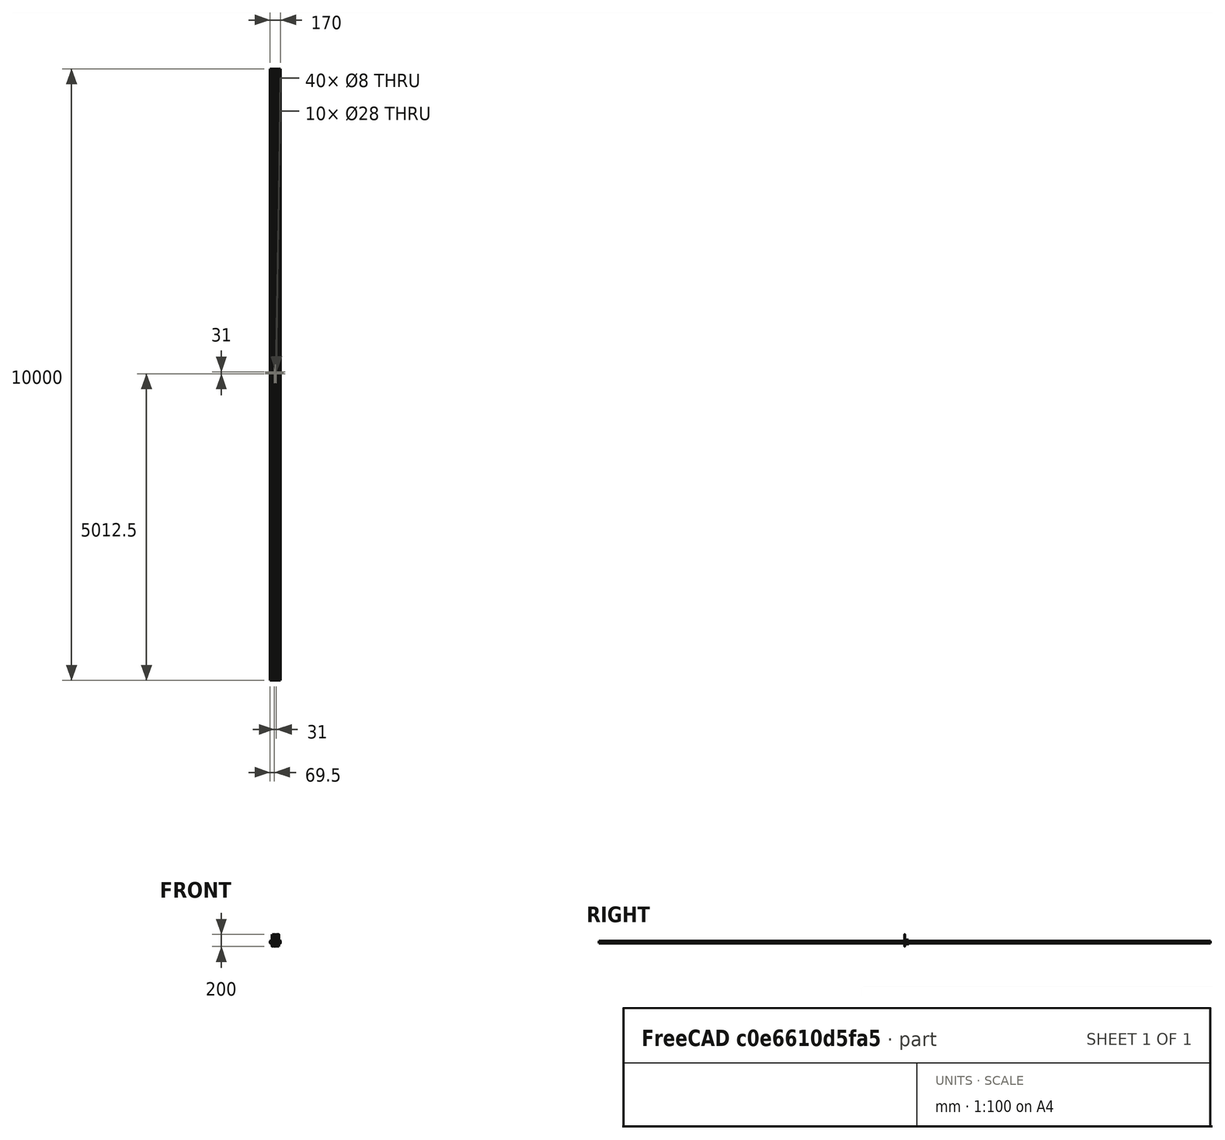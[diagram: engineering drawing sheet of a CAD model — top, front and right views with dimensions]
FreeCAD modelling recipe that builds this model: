
FCSTD DOCUMENT  (FreeCAD 0.16R6698 (Git))
Label: z_lower_left_v2.5
License: All rights reserved
LicenseURL: http://en.wikipedia.org/wiki/All_rights_reserved
objects: Sketcher::SketchObject×30, Drawing::FeatureViewPython×30, PartDesign::Pocket×23, PartDesign::Fillet×14, PartDesign::Pad×7, Drawing::FeatureViewPart×6, Drawing::FeaturePage×1, Part::Mirroring×1
note: 105 computed .brp shape members not serialized (recipe doc carries the construction recipe); baked Part::Feature solids carry a one-line shape summary decoded from their .brp

FEATURE [Sketcher::SketchObject] Sketch
  sketch-geometry (19):
    g0: LineSegment StartX=-45 StartY=23 StartZ=0 EndX=27 EndY=23 EndZ=0
    g1: LineSegment StartX=65 StartY=-28 StartZ=0 EndX=-65 EndY=-28 EndZ=0
    g2: LineSegment StartX=-65 StartY=-28 StartZ=0 EndX=-65 EndY=-20.6 EndZ=0
    g3: Circle CenterX=0 CenterY=0 CenterZ=0 NormalX=0 NormalY=0 NormalZ=1 Radius=9
    g4: Circle CenterX=-50 CenterY=0 CenterZ=0 NormalX=0 NormalY=0 NormalZ=1 Radius=6
    g5: LineSegment StartX=-65 StartY=-15.4 StartZ=0 EndX=-67 EndY=-15.575 EndZ=0
    g6: LineSegment StartX=-67 StartY=-15.575 StartZ=0 EndX=-67 EndY=-19.375 EndZ=0
    g7: LineSegment StartX=-67 StartY=-19.375 StartZ=0 EndX=-65 EndY=-20.6 EndZ=0
    g8: LineSegment StartX=-65 StartY=-15.4 StartZ=0 EndX=-65 EndY=3 EndZ=0
    g9: LineSegment [constr] StartX=-95 StartY=-18 StartZ=0 EndX=75 EndY=-18 EndZ=0
    g10: LineSegment StartX=65 StartY=-15.4 StartZ=0 EndX=67 EndY=-15.575 EndZ=0
    g11: LineSegment StartX=67 StartY=-15.575 StartZ=0 EndX=67 EndY=-19.375 EndZ=0
    g12: LineSegment StartX=67 StartY=-19.375 StartZ=0 EndX=65 EndY=-20.6 EndZ=0
    g13: LineSegment StartX=65 StartY=-28 StartZ=0 EndX=65 EndY=-20.6 EndZ=0
    g14: LineSegment StartX=65 StartY=-8 StartZ=0 EndX=65 EndY=-15.4 EndZ=0
    g15: LineSegment StartX=65 StartY=-8 StartZ=0 EndX=42 EndY=-8 EndZ=0
    g16: LineSegment StartX=27 StartY=23 StartZ=0 EndX=27 EndY=7 EndZ=0
    g17: ArcOfCircle CenterX=42 CenterY=7 CenterZ=0 NormalX=0 NormalY=0 NormalZ=1 Radius=15 StartAngle=3.14159 EndAngle=4.71239
    g18: ArcOfCircle CenterX=-45 CenterY=3 CenterZ=0 NormalX=0 NormalY=0 NormalZ=1 Radius=20 StartAngle=1.5708 EndAngle=3.14159
  constraints (54):
    c: Coincident(g1,g2)
    c: Horizontal(g0)
    c: Horizontal(g1)
    c: Vertical(g2)
    c: Coincident(g3,g-1)
    c: Radius(g3) = 9
    c: PointOnObject(g4,g-1)
    c: Radius(g4) = 6
    c: DistanceX(g-1,g4) = -50
    c: Angle(g5,g2) = 1.48353
    c: Coincident(g6,g5)
    c: Vertical(g6)
    c: Coincident(g6,g7)
    c: Coincident(g2,g7)
    c: Coincident(g8,g5)
    c: Tangent(g2,g8)
    c: DistanceX(g5,g5) = -2
    c: Horizontal(g9)
    c: DistanceY(g1,g9) = 10
    c: DistanceX(g-1,g9) = -95
    c: Distance(g9) = 170
    c: Coincident(g10,g11)
    c: Coincident(g11,g12)
    c: Vertical(g14)
    c: Vertical(g13)
    c: DistanceX(g-1,g1) = 65
    c: DistanceY(g9,g10) = 2.6
    c: Vertical(g11)
    c: DistanceX(g1,g11) = 2
    c: Coincident(g10,g14)
    c: Angle(g10,g14) = 1.65806
    c: Coincident(g1,g13)
    c: Coincident(g12,g13)
    c: DistanceY(g10,g12) = -5.2
    c: DistanceY(g-1,g1) = -28
    c: Distance(g10,g11) = 3.8
    c: Distance(g1,g15) = 20
    c: Horizontal(g15)
    c: Vertical(g16)
    c: Coincident(g0,g16)
    c: Coincident(g14,g15)
    c: DistanceX(g-1,g0) = 27
    c: DistanceY(g-1,g0) = 23
    c: PointOnObject(g10,g13)
    c: Tangent(g16,g17) = -1.5708
    c: Tangent(g15,g17) = 1.5708
    c: Radius(g17) = 15
    c: Tangent(g0,g18) = 1.5708
    c: Tangent(g8,g18) = 1.5708
    c: Radius(g18) = 20
    c: DistanceX(g-1,g8) = -65
    c: DistanceY(g9,g5) = 2.6
    c: DistanceY(g5,g2) = -5.2
    c: DistanceY(g5,g6) = -3.8
FEATURE [PartDesign::Pad] Pad
  Length = 70
  Length2 = 100
  Sketch = -> Sketch
  Type = 0
FEATURE [Sketcher::SketchObject] Sketch001
  ExternalGeometry = -> [Pad]
  Placement = pos=(0,-28,0) rot=(1,0,0;1.5708rad)
  Support = -> Pad [Face10]
  sketch-geometry (36):
    g0: LineSegment StartX=-17 StartY=53.35 StartZ=0 EndX=17 EndY=53.35 EndZ=0
    g1: LineSegment StartX=22 StartY=48.35 StartZ=0 EndX=22 EndY=16.35 EndZ=0
    g2: LineSegment StartX=17 StartY=11.35 StartZ=0 EndX=-17 EndY=11.35 EndZ=0
    g3: LineSegment StartX=-22 StartY=16.35 StartZ=0 EndX=-22 EndY=48.35 EndZ=0
    g4: LineSegment StartX=-55 StartY=53.85 StartZ=0 EndX=-32 EndY=53.85 EndZ=0
    g5: LineSegment StartX=-27 StartY=48.85 StartZ=0 EndX=-27 EndY=16.35 EndZ=0
    g6: LineSegment StartX=-32 StartY=11.35 StartZ=0 EndX=-55 EndY=11.35 EndZ=0
    g7: LineSegment StartX=-60 StartY=16.35 StartZ=0 EndX=-60 EndY=48.85 EndZ=0
    g8: LineSegment StartX=32 StartY=53.85 StartZ=0 EndX=55 EndY=53.85 EndZ=0
    g9: LineSegment StartX=60 StartY=48.85 StartZ=0 EndX=60 EndY=16.35 EndZ=0
    g10: LineSegment StartX=55 StartY=11.35 StartZ=0 EndX=32 EndY=11.35 EndZ=0
    g11: LineSegment StartX=27 StartY=16.35 StartZ=0 EndX=27 EndY=48.85 EndZ=0
    g12: LineSegment StartX=66.2175 StartY=52 StartZ=0 EndX=85 EndY=52 EndZ=0
    g13: LineSegment StartX=85 StartY=52 StartZ=0 EndX=85 EndY=15 EndZ=0
    g14: LineSegment StartX=85 StartY=15 StartZ=0 EndX=66 EndY=15 EndZ=0
    g15: LineSegment StartX=65 StartY=16 StartZ=0 EndX=65 EndY=51.0122 EndZ=0
    g16: LineSegment StartX=-85 StartY=52 StartZ=0 EndX=-66.434 EndY=52 EndZ=0
    g17: LineSegment StartX=-65 StartY=50.9699 StartZ=0 EndX=-65 EndY=16 EndZ=0
    g18: LineSegment StartX=-66 StartY=15 StartZ=0 EndX=-85 EndY=15 EndZ=0
    g19: LineSegment StartX=-85 StartY=15 StartZ=0 EndX=-85 EndY=52 EndZ=0
    g20: ArcOfCircle CenterX=-65.991 CenterY=51.1035 CenterZ=0 NormalX=0 NormalY=0 NormalZ=1 Radius=1 StartAngle=6.14926 EndAngle=8.31288
    g21: ArcOfCircle CenterX=-66 CenterY=16 CenterZ=0 NormalX=0 NormalY=0 NormalZ=1 Radius=1 StartAngle=4.71239 EndAngle=6.28319
    g22: ArcOfCircle CenterX=66 CenterY=16 CenterZ=0 NormalX=0 NormalY=0 NormalZ=1 Radius=1 StartAngle=3.14159 EndAngle=4.71239
    g23: ArcOfCircle CenterX=65.9999 CenterY=51.024 CenterZ=0 NormalX=0 NormalY=0 NormalZ=1 Radius=1 StartAngle=1.35147 EndAngle=3.15339
    g24: ArcOfCircle CenterX=-17 CenterY=16.35 CenterZ=0 NormalX=0 NormalY=0 NormalZ=1 Radius=5 StartAngle=3.14159 EndAngle=4.71239
    g25: ArcOfCircle CenterX=17 CenterY=16.35 CenterZ=0 NormalX=0 NormalY=0 NormalZ=1 Radius=5 StartAngle=4.71239 EndAngle=6.28319
    g26: ArcOfCircle CenterX=17 CenterY=48.35 CenterZ=0 NormalX=0 NormalY=0 NormalZ=1 Radius=5 StartAngle=0 EndAngle=1.5708
    g27: ArcOfCircle CenterX=-17 CenterY=48.35 CenterZ=0 NormalX=0 NormalY=0 NormalZ=1 Radius=5 StartAngle=1.5708 EndAngle=3.14159
    g28: ArcOfCircle CenterX=32 CenterY=16.35 CenterZ=0 NormalX=0 NormalY=0 NormalZ=1 Radius=5 StartAngle=3.14159 EndAngle=4.71239
    g29: ArcOfCircle CenterX=32 CenterY=48.85 CenterZ=0 NormalX=0 NormalY=0 NormalZ=1 Radius=5 StartAngle=1.5708 EndAngle=3.14159
    g30: ArcOfCircle CenterX=55 CenterY=48.85 CenterZ=0 NormalX=0 NormalY=0 NormalZ=1 Radius=5 StartAngle=0 EndAngle=1.5708
    g31: ArcOfCircle CenterX=55 CenterY=16.35 CenterZ=0 NormalX=0 NormalY=0 NormalZ=1 Radius=5 StartAngle=4.71239 EndAngle=6.28319
    g32: ArcOfCircle CenterX=-32 CenterY=48.85 CenterZ=0 NormalX=0 NormalY=0 NormalZ=1 Radius=5 StartAngle=0 EndAngle=1.5708
    g33: ArcOfCircle CenterX=-55 CenterY=48.85 CenterZ=0 NormalX=0 NormalY=0 NormalZ=1 Radius=5 StartAngle=1.5708 EndAngle=3.14159
    g34: ArcOfCircle CenterX=-55 CenterY=16.35 CenterZ=0 NormalX=0 NormalY=0 NormalZ=1 Radius=5 StartAngle=3.14159 EndAngle=4.71239
    g35: ArcOfCircle CenterX=-32 CenterY=16.35 CenterZ=0 NormalX=0 NormalY=0 NormalZ=1 Radius=5 StartAngle=4.71239 EndAngle=6.28319
  constraints (92):
    c: Coincident(g13,g12)
    c: Coincident(g23,g12)
    c: Coincident(g14,g13)
    c: Coincident(g14,g22)
    c: Coincident(g22,g15)
    c: Coincident(g23,g15)
    c: Coincident(g19,g16)
    c: Coincident(g20,g16)
    c: Coincident(g20,g17)
    c: Coincident(g21,g17)
    c: Coincident(g19,g18)
    c: Coincident(g21,g18)
    c: Distance(g-1,g2) = 11.35
    c: Distance(g-1,g1) = 22
    c: Horizontal(g4)
    c: Horizontal(g6)
    c: Horizontal(g2)
    c: Horizontal(g0)
    c: Horizontal(g8)
    c: Horizontal(g10)
    c: Vertical(g7)
    c: Vertical(g5)
    c: Vertical(g3)
    c: Vertical(g1)
    c: Vertical(g11)
    c: Vertical(g9)
    c: Tangent(g3,g24) = 1.5708
    c: Tangent(g2,g24) = 1.5708
    c: Tangent(g2,g25) = 1.5708
    c: Tangent(g1,g25) = 1.5708
    c: Tangent(g0,g26) = 1.5708
    c: Tangent(g1,g26) = 1.5708
    c: Tangent(g0,g27) = 1.5708
    c: Tangent(g3,g27) = 1.5708
    c: Radius(g27) = 5
    c: Equal(g27,g26)
    c: Equal(g26,g25)
    c: Equal(g25,g24)
    c: DistanceX(g1,g3) = -44
    c: Distance(g1,g11) = 5
    c: Tangent(g11,g28) = 1.5708
    c: Tangent(g10,g28) = 1.5708
    c: Tangent(g11,g29) = 1.5708
    c: Tangent(g8,g29) = 1.5708
    c: Tangent(g8,g30) = 1.5708
    c: Tangent(g9,g30) = 1.5708
    c: Tangent(g9,g31) = 1.5708
    c: Tangent(g10,g31) = 1.5708
    c: Equal(g27,g29)
    c: Equal(g29,g30)
    c: Equal(g30,g31)
    c: Equal(g31,g28)
    c: DistanceX(g11,g9) = 33
    c: DistanceY(g-1,g10) = 11.35
    c: DistanceY(g0,g2) = -42
    c: DistanceY(g8,g10) = -42.5
    c: Tangent(g4,g32) = 1.5708
    c: Tangent(g5,g32) = 1.5708
    c: Tangent(g4,g33) = 1.5708
    c: Tangent(g7,g33) = 1.5708
    c: Tangent(g7,g34) = 1.5708
    c: Tangent(g6,g34) = 1.5708
    c: Tangent(g6,g35) = 1.5708
    c: Tangent(g5,g35) = 1.5708
    c: Equal(g27,g32)
    c: Equal(g32,g33)
    c: Equal(g33,g34)
    c: Equal(g34,g35)
    c: DistanceX(g3,g5) = -5
    c: DistanceX(g5,g7) = -33
    c: DistanceY(g-1,g6) = 11.35
    c: DistanceY(g6,g4) = 42.5
    c: DistanceY(g-1,g13) = 15
    c: DistanceY(g-1,g18) = 15
    c: DistanceX(g-1,g15) = 65
    c: DistanceX(g-1,g17) = -65
    c: Distance(g13) = 37
    c: Distance(g19) = 37
    c: Radius(g21) = 1
    c: DistanceX(g-1,g13) = 85
    c: DistanceX(g-1,g18) = -85
    c: Vertical(g15)
    c: Vertical(g17)
    c: Vertical(g19)
    c: Vertical(g13)
    c: Horizontal(g18)
    c: Horizontal(g16)
    c: Horizontal(g12)
    c: Horizontal(g14)
    c: Equal(g21,g20)
    c: Equal(g21,g22)
    c: Equal(g22,g23)
FEATURE [PartDesign::Pocket] Pocket
  Length = 5
  Midplane = true
  Sketch = -> Sketch001
  Type = 1
FEATURE [Sketcher::SketchObject] Sketch011
  Placement = pos=(0,0,70) rot=(0,0,1;0rad)
  Support = -> Pocket [Face3]
  sketch-geometry (13):
    g0: LineSegment StartX=-75 StartY=35 StartZ=0 EndX=75 EndY=35 EndZ=0
    g1: LineSegment StartX=75 StartY=35 StartZ=0 EndX=75 EndY=-35 EndZ=0
    g2: LineSegment StartX=75 StartY=-35 StartZ=0 EndX=-40 EndY=-35 EndZ=0
    g3: LineSegment StartX=-75 StartY=-35 StartZ=0 EndX=-75 EndY=35 EndZ=0
    g4: LineSegment [constr] StartX=-75 StartY=0 StartZ=0 EndX=75 EndY=0 EndZ=0
    g5: LineSegment [constr] StartX=0 StartY=35 StartZ=0 EndX=0 EndY=-35 EndZ=0
    g6: ArcOfCircle [constr] CenterX=-50 CenterY=0 CenterZ=0 NormalX=0 NormalY=0 NormalZ=1 Radius=10 StartAngle=3.14159 EndAngle=6.28319
    g7: ArcOfCircle [constr] CenterX=0 CenterY=0 CenterZ=0 NormalX=0 NormalY=0 NormalZ=1 Radius=16 StartAngle=0 EndAngle=3.14159
    g8: LineSegment StartX=-60 StartY=-2e-12 StartZ=0 EndX=-60 EndY=-35 EndZ=0
    g9: LineSegment StartX=-40 StartY=0 StartZ=0 EndX=-40 EndY=-35 EndZ=0
    g10: LineSegment StartX=-60 StartY=-35 StartZ=0 EndX=-75 EndY=-35 EndZ=0
    g11: Circle CenterX=0 CenterY=0 CenterZ=0 NormalX=0 NormalY=0 NormalZ=1 Radius=16
    g12: ArcOfCircle CenterX=-50 CenterY=0 CenterZ=0 NormalX=0 NormalY=0 NormalZ=1 Radius=10 StartAngle=0 EndAngle=3.14159
  constraints (42):
    c: Coincident(g1,g0)
    c: Coincident(g0,g3)
    c: Coincident(g2,g1)
    c: Coincident(g10,g3)
    c: Vertical(g5)
    c: Horizontal(g4)
    c: PointOnObject(g-1,g4)
    c: PointOnObject(g-1,g5)
    c: Radius(g6) = 10
    c: PointOnObject(g6,g4)
    c: DistanceX(g-1,g6) = -50
    c: PointOnObject(g6,g4)
    c: PointOnObject(g6,g4)
    c: Radius(g7) = 16
    c: Coincident(g7,g-1)
    c: Vertical(g8)
    c: Vertical(g9)
    c: Horizontal(g2)
    c: Horizontal(g0)
    c: Vertical(g3)
    c: Vertical(g1)
    c: Coincident(g10,g8)
    c: Tangent(g2,g10)
    c: Distance(g-1,g2) = 35
    c: DistanceX(g-1,g1) = 75
    c: Distance(g0) = 150
    c: Distance(g1) = 70
    c: PointOnObject(g4,g1)
    c: PointOnObject(g4,g3)
    c: PointOnObject(g5,g0)
    c: PointOnObject(g7,g4)
    c: PointOnObject(g7,g4)
    c: Coincident(g7,g11)
    c: Radius(g11) = 16
    c: Coincident(g2,g9)
    c: Coincident(g6,g12)
    c: PointOnObject(g12,g4)
    c: PointOnObject(g12,g4)
    c: PointOnObject(g9,g4)
    c: Equal(g12,g6)
    c: DistanceX(g5,g2) = -40
    c: Coincident(g6,g8)
FEATURE [PartDesign::Pocket] Pocket001
  Length = 10
  Sketch = -> Sketch011
  Type = 0
FEATURE [Sketcher::SketchObject] Sketch055
  Placement = pos=(0,0,0) rot=(1,0,0;3.14159rad)
  Support = -> Pocket001 [Face2]
  sketch-geometry (8):
    g0: LineSegment StartX=-75 StartY=40 StartZ=0 EndX=-60 EndY=40 EndZ=0
    g1: LineSegment StartX=75 StartY=40 StartZ=0 EndX=75 EndY=-40 EndZ=0
    g2: LineSegment StartX=75 StartY=-40 StartZ=0 EndX=-75 EndY=-40 EndZ=0
    g3: LineSegment StartX=-75 StartY=-40 StartZ=0 EndX=-75 EndY=40 EndZ=0
    g4: ArcOfCircle CenterX=-50 CenterY=0 CenterZ=0 NormalX=0 NormalY=0 NormalZ=1 Radius=10 StartAngle=3.14159 EndAngle=6.28319
    g5: LineSegment StartX=-40 StartY=40 StartZ=0 EndX=-40 EndY=4e-12 EndZ=0
    g6: LineSegment StartX=-60 StartY=40 StartZ=0 EndX=-60 EndY=-2e-12 EndZ=0
    g7: LineSegment StartX=-40 StartY=40 StartZ=0 EndX=75 EndY=40 EndZ=0
  constraints (24):
    c: Coincident(g7,g1)
    c: Coincident(g1,g2)
    c: Coincident(g3,g0)
    c: Horizontal(g0)
    c: Horizontal(g2)
    c: Vertical(g1)
    c: Vertical(g3)
    c: DistanceY(g-1,g1) = -40
    c: DistanceY(g1) = -80
    c: DistanceX(g-1,g7) = 75
    c: PointOnObject(g5,g-1)
    c: Radius(g4) = 10
    c: Coincident(g2,g3)
    c: Vertical(g6)
    c: Vertical(g5)
    c: DistanceX(g-1,g4) = -50
    c: PointOnObject(g4,g6)
    c: Tangent(g0,g7)
    c: Coincident(g6,g0)
    c: Coincident(g5,g7)
    c: DistanceX(g2) = -150
    c: PointOnObject(g4,g-1)
    c: Coincident(g4,g6)
    c: Coincident(g4,g5)
FEATURE [PartDesign::Pocket] Pocket002
  Length = 6
  Sketch = -> Sketch055
  Type = 0
FEATURE [Sketcher::SketchObject] Sketch029
  Placement = pos=(0,0,53.85) rot=(1,0,0;3.14159rad)
  Support = -> Pocket002 [Face6]
  sketch-geometry (8):
    g0: Circle CenterX=-15.5 CenterY=15.5 CenterZ=0 NormalX=0 NormalY=0 NormalZ=1 Radius=4
    g1: Circle CenterX=15.5 CenterY=15.5 CenterZ=0 NormalX=0 NormalY=0 NormalZ=1 Radius=4
    g2: Circle CenterX=-15.5 CenterY=-15.5 CenterZ=0 NormalX=0 NormalY=0 NormalZ=1 Radius=4
    g3: Circle CenterX=15.5 CenterY=-15.5 CenterZ=0 NormalX=0 NormalY=0 NormalZ=1 Radius=4
    g4: LineSegment [constr] StartX=-15.5 StartY=15.5 StartZ=0 EndX=15.5 EndY=15.5 EndZ=0
    g5: LineSegment [constr] StartX=15.5 StartY=15.5 StartZ=0 EndX=15.5 EndY=-15.5 EndZ=0
    g6: LineSegment [constr] StartX=15.5 StartY=-15.5 StartZ=0 EndX=-15.5 EndY=-15.5 EndZ=0
    g7: LineSegment [constr] StartX=-15.5 StartY=-15.5 StartZ=0 EndX=-15.5 EndY=15.5 EndZ=0
  constraints (20):
    c: Radius(g0) = 4
    c: Equal(g0,g1)
    c: Equal(g1,g2)
    c: Equal(g2,g3)
    c: Coincident(g4,g5)
    c: Coincident(g5,g6)
    c: Coincident(g6,g7)
    c: Coincident(g7,g4)
    c: Horizontal(g4)
    c: Horizontal(g6)
    c: Vertical(g5)
    c: Vertical(g7)
    c: DistanceY(g-1,g4) = 15.5
    c: Distance(g5) = 31
    c: DistanceX(g4) = 31
    c: DistanceX(g-1,g4) = 15.5
    c: Coincident(g0,g4)
    c: Coincident(g1,g4)
    c: Coincident(g3,g5)
    c: Coincident(g2,g6)
FEATURE [PartDesign::Pocket] Pocket003
  Length = 8
  Sketch = -> Sketch029
  Type = 0
FEATURE [Sketcher::SketchObject] Sketch033
  Placement = pos=(0,0,6) rot=(1,0,0;3.14159rad)
  Support = -> Pocket003 [Face2]
  sketch-geometry (11):
    g0: Circle CenterX=-15.5 CenterY=15.25 CenterZ=0 NormalX=0 NormalY=0 NormalZ=1 Radius=2.1
    g1: Circle CenterX=-15.5 CenterY=-15.75 CenterZ=0 NormalX=0 NormalY=0 NormalZ=1 Radius=2.1
    g2: Circle CenterX=15.5 CenterY=15.25 CenterZ=0 NormalX=0 NormalY=0 NormalZ=1 Radius=2.1
    g3: Circle CenterX=15.5 CenterY=-15.75 CenterZ=0 NormalX=0 NormalY=0 NormalZ=1 Radius=2.1
    g4: Circle CenterX=0 CenterY=0 CenterZ=0 NormalX=0 NormalY=0 NormalZ=1 Radius=14
    g5: LineSegment [constr] StartX=0 StartY=35 StartZ=0 EndX=0 EndY=-35 EndZ=0
    g6: LineSegment [constr] StartX=-35 StartY=0 StartZ=0 EndX=35 EndY=0 EndZ=0
    g7: LineSegment [constr] StartX=-15.5 StartY=15.25 StartZ=0 EndX=15.5 EndY=15.25 EndZ=0
    g8: LineSegment [constr] StartX=15.5 StartY=15.25 StartZ=0 EndX=15.5 EndY=-15.75 EndZ=0
    g9: LineSegment [constr] StartX=15.5 StartY=-15.75 StartZ=0 EndX=-15.5 EndY=-15.75 EndZ=0
    g10: LineSegment [constr] StartX=-15.5 StartY=-15.75 StartZ=0 EndX=-15.5 EndY=15.25 EndZ=0
  constraints (30):
    c: Radius(g3) = 2.1
    c: Equal(g3,g2)
    c: Equal(g2,g1)
    c: Equal(g1,g0)
    c: Radius(g4) = 14
    c: Horizontal(g6)
    c: Vertical(g5)
    c: PointOnObject(g-1,g5)
    c: PointOnObject(g-1,g6)
    c: Coincident(g4,g-1)
    c: Coincident(g7,g8)
    c: Coincident(g8,g9)
    c: Coincident(g9,g10)
    c: Coincident(g10,g7)
    c: Horizontal(g7)
    c: Horizontal(g9)
    c: Vertical(g8)
    c: Vertical(g10)
    c: DistanceX(g-1,g8) = 15.5
    c: Distance(g9) = 31
    c: DistanceY(g-1,g8) = -15.75
    c: Distance(g8) = 31
    c: Coincident(g1,g9)
    c: Coincident(g3,g8)
    c: Coincident(g2,g8)
    c: Coincident(g0,g7)
    c: Distance(g6) = 70
    c: DistanceX(g-1,g6) = -35
    c: Distance(g5) = 70
    c: DistanceY(g-1,g5) = -35
FEATURE [PartDesign::Pocket] Pocket004
  Length = 10
  Sketch = -> Sketch033
  Type = 0
FEATURE [Sketcher::SketchObject] Sketch040
  Placement = pos=(0,0,70) rot=(0,0,1;0rad)
  Support = -> Pocket004 [Face82]
  sketch-geometry (1):
    g0: Circle CenterX=0 CenterY=0 CenterZ=0 NormalX=0 NormalY=0 NormalZ=1 Radius=11.2
  constraints (2):
    c: Radius(g0) = 11.2
    c: Coincident(g0,g-1)
FEATURE [PartDesign::Pocket] Pocket005
  Length = 14.6
  Sketch = -> Sketch040
  Type = 0
FEATURE [Sketcher::SketchObject] Sketch056
  Placement = pos=(0,0,70) rot=(0,0,1;0rad)
  Support = -> Pocket005 [Face82]
  sketch-geometry (1):
    g0: Circle CenterX=0 CenterY=0 CenterZ=0 NormalX=0 NormalY=0 NormalZ=1 Radius=20
  constraints (2):
    c: Coincident(g0,g-1)
    c: Radius(g0) = 20
FEATURE [PartDesign::Pocket] Pocket006
  Length = 7.6
  Sketch = -> Sketch056
  Type = 0
FEATURE [Sketcher::SketchObject] Sketch043
  Placement = pos=(-65,0,0) rot=(0.57735,-0.57735,-0.57735;2.0944rad)
  Support = -> Pocket006 [Face27]
  sketch-geometry (3):
    g0: LineSegment [constr] StartX=18 StartY=43.5 StartZ=0 EndX=18 EndY=23.5 EndZ=0
    g1: Circle CenterX=18 CenterY=43.5 CenterZ=0 NormalX=0 NormalY=0 NormalZ=1 Radius=3
    g2: Circle CenterX=18 CenterY=23.5 CenterZ=0 NormalX=0 NormalY=0 NormalZ=1 Radius=3
  constraints (7):
    c: Vertical(g0)
    c: DistanceY(g-1,g0) = 23.5
    c: DistanceY(g0,g0) = 20
    c: Coincident(g2,g0)
    c: Coincident(g1,g0)
    c: Radius(g2) = 3
    c: Equal(g2,g1)
FEATURE [PartDesign::Pocket] Pocket007
  Length = 8
  Sketch = -> Sketch043
  Type = 0
FEATURE [Sketcher::SketchObject] Sketch053
  Placement = pos=(65,0,0) rot=(0.57735,0.57735,0.57735;2.0944rad)
  Support = -> Pocket007 [Face21]
  sketch-geometry (3):
    g0: Circle CenterX=-18 CenterY=43.5 CenterZ=0 NormalX=0 NormalY=0 NormalZ=1 Radius=3
    g1: Circle CenterX=-18 CenterY=23.5 CenterZ=0 NormalX=0 NormalY=0 NormalZ=1 Radius=3
    g2: LineSegment [constr] StartX=-18 StartY=43.5 StartZ=0 EndX=-18 EndY=23.5 EndZ=0
  constraints (7):
    c: Vertical(g2)
    c: Coincident(g2,g1)
    c: Coincident(g2,g0)
    c: DistanceY(g-1,g1) = 23.5
    c: DistanceY(g2) = -20
    c: Radius(g1) = 3
    c: Equal(g1,g0)
FEATURE [PartDesign::Pocket] Pocket008
  Length = 8
  Sketch = -> Sketch053
  Type = 0
FEATURE [Sketcher::SketchObject] Sketch057
  Placement = pos=(-60,0,0) rot=(0.57735,-0.57735,-0.57735;2.0944rad)
  Support = -> Pocket008 [Face41]
  sketch-geometry (1):
    g0: Circle CenterX=0 CenterY=65 CenterZ=0 NormalX=0 NormalY=0 NormalZ=1 Radius=2.1
  constraints (3):
    c: Radius(g0) = 2.1
    c: DistanceX(g-1,g0) = 0
    c: DistanceY(g-1,g0) = 65
FEATURE [PartDesign::Pocket] Pocket009
  Length = 8
  Sketch = -> Sketch057
  Type = 0
FEATURE [PartDesign::Fillet] Fillet
  Radius = 1
FEATURE [PartDesign::Fillet] Fillet001
  Base = -> Fillet [Edge15]
  Radius = 1
FEATURE [PartDesign::Fillet] Fillet002
  Base = -> Fillet001 [Edge185]
  Radius = 1
FEATURE [PartDesign::Fillet] Fillet003
  Base = -> Fillet002 [Edge85]
  Radius = 1
FEATURE [PartDesign::Fillet] Fillet004
  Base = -> Fillet003 [Edge153]
  Radius = 1
FEATURE [PartDesign::Fillet] Fillet005
  Base = -> Fillet004 [Edge12,Edge4,Edge5]
  Radius = 1
FEATURE [PartDesign::Fillet] Fillet006
  Base = -> Fillet005 [Edge24,Edge9,Edge17]
  Radius = 1
FEATURE [Sketcher::SketchObject] Sketch062
  Placement = pos=(0,0,60) rot=(0,0,1;0rad)
  Support = -> Fillet006 [Face64]
  sketch-geometry (12):
    g0: Circle CenterX=-45 CenterY=-28 CenterZ=0 NormalX=0 NormalY=0 NormalZ=1 Radius=0.5
    g1: Circle CenterX=-55 CenterY=-28 CenterZ=0 NormalX=0 NormalY=0 NormalZ=1 Radius=0.5
    g2: Circle CenterX=-35 CenterY=-28 CenterZ=0 NormalX=0 NormalY=0 NormalZ=1 Radius=0.5
    g3: Circle CenterX=-25 CenterY=-28 CenterZ=0 NormalX=0 NormalY=0 NormalZ=1 Radius=0.5
    g4: Circle CenterX=25 CenterY=-28 CenterZ=0 NormalX=0 NormalY=0 NormalZ=1 Radius=0.5
    g5: Circle CenterX=35 CenterY=-28 CenterZ=0 NormalX=0 NormalY=0 NormalZ=1 Radius=0.5
    g6: Circle CenterX=45 CenterY=-28 CenterZ=0 NormalX=0 NormalY=0 NormalZ=1 Radius=0.5
    g7: Circle CenterX=55 CenterY=-28 CenterZ=0 NormalX=0 NormalY=0 NormalZ=1 Radius=0.5
    g8: Circle CenterX=15 CenterY=-28 CenterZ=0 NormalX=0 NormalY=0 NormalZ=1 Radius=0.5
    g9: Circle CenterX=5 CenterY=-28 CenterZ=0 NormalX=0 NormalY=0 NormalZ=1 Radius=0.5
    g10: Circle CenterX=-5 CenterY=-28 CenterZ=0 NormalX=0 NormalY=0 NormalZ=1 Radius=0.5
    g11: Circle CenterX=-15 CenterY=-28 CenterZ=0 NormalX=0 NormalY=0 NormalZ=1 Radius=0.5
  constraints (24):
    c: Radius(g0) = 0.5
    c: DistanceX(g-1,g0) = -45
    c: DistanceX(g0,g1) = -10
    c: Equal(g0,g1)
    c: Equal(g0,g2)
    c: DistanceX(g0,g2) = 10
    c: DistanceX(g2,g3) = 10
    c: Equal(g0,g3)
    c: DistanceX(g4,g5) = 10
    c: DistanceX(g3,g11) = 10
    c: DistanceX(g11,g10) = 10
    c: Equal(g3,g11)
    c: Equal(g11,g10)
    c: DistanceX(g10,g9) = 10
    c: DistanceX(g9,g8) = 10
    c: Equal(g10,g9)
    c: Equal(g9,g8)
    c: Equal(g8,g4)
    c: Equal(g4,g5)
    c: Equal(g5,g6)
    c: Equal(g6,g7)
    c: DistanceX(g8,g4) = 10
    c: DistanceX(g5,g6) = 10
    c: DistanceX(g7,g6) = -10
FEATURE [PartDesign::Pocket] Pocket010
  Length = 200
  Midplane = true
  Sketch = -> Sketch062
  Type = 0
FEATURE [Sketcher::SketchObject] Sketch058
  Placement = pos=(0,23,0) rot=(0,0.707107,0.707107;3.14159rad)
  Support = -> Pocket010 [Face57]
  sketch-geometry (4):
    g0: LineSegment StartX=-32.3231 StartY=47 StartZ=0 EndX=39.8959 EndY=47 EndZ=0
    g1: LineSegment StartX=39.8959 StartY=47 StartZ=0 EndX=39.8959 EndY=18 EndZ=0
    g2: LineSegment StartX=39.8959 StartY=18 StartZ=0 EndX=-32.3231 EndY=18 EndZ=0
    g3: LineSegment StartX=-32.3231 StartY=18 StartZ=0 EndX=-32.3231 EndY=47 EndZ=0
  constraints (10):
    c: Coincident(g0,g1)
    c: Coincident(g1,g2)
    c: Coincident(g2,g3)
    c: Coincident(g3,g0)
    c: Horizontal(g0)
    c: Horizontal(g2)
    c: Vertical(g1)
    c: Vertical(g3)
    c: DistanceY(g-1,g2) = 18
    c: Distance(g3) = 29
FEATURE [PartDesign::Pocket] Pocket011
  Length = 5
  Sketch = -> Sketch058
  Type = 0
FEATURE [PartDesign::Fillet] Fillet007
  Base = -> Pocket011 [Edge283,Edge314]
  Radius = 1
FEATURE [PartDesign::Fillet] Fillet009
  Radius = 1
FEATURE [PartDesign::Fillet] Fillet010
  Base = -> Fillet009 [Edge52]
  Radius = 1
FEATURE [PartDesign::Fillet] Fillet011
  Base = -> Fillet010 [Edge111]
  Radius = 1
FEATURE [PartDesign::Fillet] Fillet012
  Base = -> Fillet011 [Edge365]
  Radius = 1
FEATURE [PartDesign::Fillet] Fillet013
  Base = -> Fillet012 [Edge195,Edge517,Edge301]
  Radius = 1
FEATURE [PartDesign::Fillet] Fillet014
  Base = -> Fillet013 [Edge46]
  Radius = 1
FEATURE [Sketcher::SketchObject] Sketch066
  Placement = pos=(27,0,0) rot=(0.57735,0.57735,0.57735;2.0944rad)
  Support = -> Fillet014 [Face109]
  sketch-geometry (4):
    g0: ArcOfCircle CenterX=1 CenterY=41.5 CenterZ=0 NormalX=0 NormalY=0 NormalZ=1 Radius=7 StartAngle=0 EndAngle=3.14159
    g1: ArcOfCircle CenterX=1 CenterY=23.5 CenterZ=0 NormalX=0 NormalY=0 NormalZ=1 Radius=7 StartAngle=3.14159 EndAngle=6.28319
    g2: LineSegment StartX=-6 StartY=41.5 StartZ=0 EndX=-6 EndY=23.5 EndZ=0
    g3: LineSegment StartX=8 StartY=41.5 StartZ=0 EndX=8 EndY=23.5 EndZ=0
  constraints (10):
    c: Tangent(g0,g3) = 1.5708
    c: Tangent(g0,g2) = -1.5708
    c: Tangent(g2,g1) = -1.5708
    c: Tangent(g3,g1) = 1.5708
    c: Vertical(g2)
    c: Equal(g0,g1)
    c: DistanceY(g-1,g1) = 23.5
    c: DistanceY(g3) = -18
    c: Radius(g1) = 7
    c: DistanceX(g-1,g1) = 1
FEATURE [PartDesign::Pocket] Pocket012
  Length = 70
  Sketch = -> Sketch066
  Type = 0
FEATURE [Sketcher::SketchObject] Sketch064
  Placement = pos=(60,0,0) rot=(0.57735,-0.57735,-0.57735;2.0944rad)
  Support = -> Pocket012 [Face233]
  sketch-geometry (2):
    g0: Circle CenterX=18 CenterY=43.5 CenterZ=0 NormalX=0 NormalY=0 NormalZ=1 Radius=6
    g1: Circle CenterX=18 CenterY=23.5 CenterZ=0 NormalX=0 NormalY=0 NormalZ=1 Radius=6
  constraints (2):
    c: Equal(g0,g1)
    c: Radius(g1) = 6
FEATURE [PartDesign::Pocket] Pocket013
  Length = 2.5
  Sketch = -> Sketch064
  Type = 0
FEATURE [Sketcher::SketchObject] Sketch065
  Placement = pos=(-60,0,0) rot=(0.57735,0.57735,0.57735;2.0944rad)
  Support = -> Pocket013 [Face59]
  sketch-geometry (2):
    g0: Circle CenterX=-18 CenterY=43.5 CenterZ=0 NormalX=0 NormalY=0 NormalZ=1 Radius=6
    g1: Circle CenterX=-18 CenterY=23.5 CenterZ=0 NormalX=0 NormalY=0 NormalZ=1 Radius=6
  constraints (2):
    c: Radius(g0) = 6
    c: Equal(g0,g1)
FEATURE [PartDesign::Pocket] Pocket014
  Length = 2.5
  Sketch = -> Sketch065
  Type = 0
FEATURE [Sketcher::SketchObject] Sketch067
  ExternalGeometry = -> [Pocket014]
  Placement = pos=(0,0,62.4) rot=(0,0,1;0rad)
  Support = -> Pocket014 [Face264]
  sketch-geometry (4):
    g0: ArcOfCircle CenterX=0 CenterY=0 CenterZ=0 NormalX=0 NormalY=0 NormalZ=1 Radius=14 StartAngle=3.91679 EndAngle=5.50799
    g1: LineSegment StartX=-10 StartY=-9.79796 StartZ=0 EndX=-10 EndY=-28 EndZ=0
    g2: LineSegment StartX=10 StartY=-9.79796 StartZ=0 EndX=10 EndY=-28 EndZ=0
    g3: LineSegment StartX=-10 StartY=-28 StartZ=0 EndX=10 EndY=-28 EndZ=0
  constraints (12):
    c: Coincident(g0,g-1)
    c: Vertical(g1)
    c: Vertical(g2)
    c: Coincident(g2,g3)
    c: Coincident(g1,g3)
    c: Horizontal(g3)
    c: Coincident(g0,g1)
    c: Coincident(g0,g2)
    c: DistanceX(g-1,g0) = 10
    c: DistanceX(g0,g0) = -20
    c: PointOnObject(g-3,g3)
    c: Radius(g0) = 14
FEATURE [PartDesign::Pad] Pad001
  Length = 5
  Length2 = 100
  Reversed = true
  Sketch = -> Sketch067
  Type = 0
FEATURE [Sketcher::SketchObject] Sketch068
  ExternalGeometry = -> [Pad001]
  Placement = pos=(0,0,62.4) rot=(0,0,1;0rad)
  Support = -> Pad001 [Face244]
  sketch-geometry (2):
    g0: Circle CenterX=-5 CenterY=-28 CenterZ=0 NormalX=0 NormalY=0 NormalZ=1 Radius=0.5
    g1: Circle CenterX=5 CenterY=-28 CenterZ=0 NormalX=0 NormalY=0 NormalZ=1 Radius=0.5
  constraints (4):
    c: Coincident(g1,g-4)
    c: Coincident(g0,g-3)
    c: PointOnObject(g-3,g0)
    c: PointOnObject(g-4,g1)
FEATURE [PartDesign::Pocket] Pocket015
  Length = 10
  Sketch = -> Sketch068
  Type = 0
FEATURE [Sketcher::SketchObject] Sketch069
  ExternalGeometry = -> [Pocket015]
  Placement = pos=(-60,0,0) rot=(0.57735,-0.57735,-0.57735;2.0944rad)
  Support = -> Pocket015 [Face85]
  sketch-geometry (1):
    g0: Circle CenterX=-22 CenterY=17 CenterZ=0 NormalX=0 NormalY=0 NormalZ=1 Radius=2.4
  constraints (2):
    c: Coincident(g0,g-3)
    c: Radius(g0) = 2.4
FEATURE [PartDesign::Pocket] Pocket016
  Length = 10
  Sketch = -> Sketch069
  Type = 0
FEATURE [Sketcher::SketchObject] Sketch070
  Placement = pos=(0,0,0) rot=(1,0,0;3.14159rad)
  sketch-geometry (1):
    g0: Circle CenterX=-50 CenterY=0 CenterZ=0 NormalX=0 NormalY=0 NormalZ=1 Radius=6.5
  constraints (1):
    c: Radius(g0) = 6.5
FEATURE [PartDesign::Pocket] Pocket017
  Length = 13
  Sketch = -> Sketch070
  Type = 0
FEATURE [Drawing::FeatureViewPart] Ortho  label="Ortho_0_0"
  Direction = (0,1,0)
  HiddenWidth = 0.15
  LineWidth = 0.35
  Rotation = -90
  Scale = 0.5
  ShowHiddenLines = false
  ShowSmoothLines = false
  Tolerance = 0.05
  ViewResult = <blob: 30758 chars omitted>
  Visible = true
  X = 155
  Y = 150
FEATURE [Drawing::FeatureViewPart] Ortho002  label="Ortho_0_-1"
  Direction = (0,0,-1)
  HiddenWidth = 0.15
  LineWidth = 0.35
  Rotation = 0
  Scale = 0.5
  ShowHiddenLines = false
  ShowSmoothLines = false
  Tolerance = 0.05
  ViewResult = <blob: 14076 chars omitted>
  Visible = true
  X = 155
  Y = 275
FEATURE [Drawing::FeatureViewPart] Ortho004  label="Ortho_1_0"
  Direction = (-1,0,0)
  HiddenWidth = 0.15
  LineWidth = 0.35
  Rotation = 90
  Scale = 0.5
  ShowHiddenLines = false
  ShowSmoothLines = false
  Tolerance = 0.05
  ViewResult = <blob: 18830 chars omitted>
  Visible = true
  X = 320
  Y = 150
FEATURE [Drawing::FeatureViewPart] Ortho005  label="Ortho_-1_0"
  Direction = (1,0,0)
  HiddenWidth = 0.15
  LineWidth = 0.35
  Rotation = -90
  Scale = 0.5
  ShowHiddenLines = false
  ShowSmoothLines = true
  Tolerance = 0.05
  ViewResult = <blob: 28246 chars omitted>
  Visible = true
  X = -10
  Y = 150
FEATURE [Drawing::FeatureViewPart] Ortho006  label="Ortho_2_0"
  Direction = (0,-1,0)
  HiddenWidth = 0.15
  LineWidth = 0.35
  Rotation = 90
  Scale = 0.5
  ShowHiddenLines = false
  ShowSmoothLines = false
  Tolerance = 0.05
  ViewResult = <blob: 19469 chars omitted>
  Visible = true
  X = 280
  Y = 150
FEATURE [Drawing::FeatureViewPart] Ortho001  label="Ortho_0_1"
  Direction = (0,0,1)
  HiddenWidth = 0.15
  LineWidth = 0.35
  Rotation = 180
  Scale = 0.5
  ShowHiddenLines = false
  ShowSmoothLines = false
  Tolerance = 0.05
  ViewResult = <blob: 15304 chars omitted>
  Visible = true
  X = 155
  Y = -10
FEATURE [Drawing::FeatureViewPython] text001  # drawing view (typed FeaturePython)
  Rotation = 0
  ViewResult = <g> <text x="193.842901" y="76.040000" font-family="inherit" font-size="5" fill="rgb(0,0,0)" text-anchor="inherit" transform="rotate(0.000000 193.842901,76.040000)" >'A'</text> </g>
  Visible = true
  X = 0
  Y = 0
  click1_x = 193.843
  click1_y = 76.04
  rotation = 0
  text = 'A'
  textRenderer_addText_color = rgb(0,0,0)
  textRenderer_addText_family = inherit
  textRenderer_addText_size = 5
FEATURE [Drawing::FeatureViewPython] text003  # drawing view (typed FeaturePython)
  Rotation = 0
  ViewResult = <g> <text x="194.827875" y="160.747771" font-family="inherit" font-size="5" fill="rgb(0,0,0)" text-anchor="inherit" transform="rotate(0.000000 194.827875,160.747771)" >'A' Right Lower Z, 'C' Left Lower Z</text> </g>
  Visible = true
  X = 0
  Y = 0
  click1_x = 194.828
  click1_y = 160.748
  rotation = 0
  text = 'A' Right Lower Z, 'C' Left Lower Z
  textRenderer_addText_color = rgb(0,0,0)
  textRenderer_addText_family = inherit
  textRenderer_addText_size = 5
FEATURE [Drawing::FeatureViewPython] text004  # drawing view (typed FeaturePython)
  Rotation = 0
  ViewResult = <g> <text x="195.024870" y="190.296994" font-family="inherit" font-size="5" fill="rgb(0,0,0)" text-anchor="inherit" transform="rotate(0.000000 195.024870,190.296994)" >'B'</text> </g>
  Visible = true
  X = 0
  Y = 0
  click1_x = 195.025
  click1_y = 190.297
  rotation = 0
  text = 'B'
  textRenderer_addText_color = rgb(0,0,0)
  textRenderer_addText_family = inherit
  textRenderer_addText_size = 5
FEATURE [Drawing::FeatureViewPython] text005  # drawing view (typed FeaturePython)
  Rotation = 0
  ViewResult = <g> <text x="97.315440" y="109.726113" font-family="inherit" font-size="5" fill="rgb(0,0,0)" text-anchor="inherit" transform="rotate(0.000000 97.315440,109.726113)" >'B' Inside Surfaces</text> </g>
  Visible = true
  X = 0
  Y = 0
  click1_x = 97.3154
  click1_y = 109.726
  rotation = 0
  text = 'B' Inside Surfaces
  textRenderer_addText_color = rgb(0,0,0)
  textRenderer_addText_family = inherit
  textRenderer_addText_size = 5
FEATURE [Drawing::FeatureViewPython] text006  # drawing view (typed FeaturePython)
  Rotation = 0
  ViewResult = <g> <text x="109.332124" y="154.640932" font-family="inherit" font-size="5" fill="rgb(0,0,0)" text-anchor="inherit" transform="rotate(0.000000 109.332124,154.640932)" >'D'</text> </g>
  Visible = true
  X = 0
  Y = 0
  click1_x = 109.332
  click1_y = 154.641
  rotation = 0
  text = 'D'
  textRenderer_addText_color = rgb(0,0,0)
  textRenderer_addText_family = inherit
  textRenderer_addText_size = 5
FEATURE [Drawing::FeatureViewPython] text007  # drawing view (typed FeaturePython)
  Rotation = 0
  ViewResult = <g> <text x="197.585802" y="109.332124" font-family="inherit" font-size="5" fill="rgb(0,0,0)" text-anchor="inherit" transform="rotate(0.000000 197.585802,109.332124)" >'D'</text> </g>
  Visible = true
  X = 0
  Y = 0
  click1_x = 197.586
  click1_y = 109.332
  rotation = 0
  text = 'D'
  textRenderer_addText_color = rgb(0,0,0)
  textRenderer_addText_family = inherit
  textRenderer_addText_size = 5
FEATURE [Drawing::FeatureViewPython] text009  # drawing view (typed FeaturePython)
  Rotation = 0
  ViewResult = <g> <text x="298.053159" y="108.347150" font-family="inherit" font-size="5" fill="rgb(0,0,0)" text-anchor="inherit" transform="rotate(0.000000 298.053159,108.347150)" >'A'</text> </g>
  Visible = true
  X = 0
  Y = 0
  click1_x = 298.053
  click1_y = 108.347
  rotation = 0
  text = 'A'
  textRenderer_addText_color = rgb(0,0,0)
  textRenderer_addText_family = inherit
  textRenderer_addText_size = 5
FEATURE [Drawing::FeatureViewPython] grabPoint001  # drawing view (typed FeaturePython)
  Rotation = 0
  ViewResult = <g> <line x1="95.7394814207" y1="139.866320594" x2="95.7394814207" y2="139.866320594" style="stroke:rgb(0,0,0);stroke-width:0.01" /> </g> 
  Visible = true
  X = 0
  Y = 0
  click1_x = 95.7395
  click1_y = 139.866
FEATURE [Drawing::FeatureViewPython] grabPoint002  # drawing view (typed FeaturePython)
  Rotation = 0
  ViewResult = <g> <line x1="179.462278959" y1="146.761139215" x2="179.462278959" y2="146.761139215" style="stroke:rgb(0,0,0);stroke-width:0.01" /> </g> 
  Visible = true
  X = 0
  Y = 0
  click1_x = 179.462
  click1_y = 146.761
FEATURE [Drawing::FeatureViewPython] grabPoint003  # drawing view (typed FeaturePython)
  Rotation = 0
  ViewResult = <g> <line x1="169.021553619" y1="176.901346329" x2="169.021553619" y2="176.901346329" style="stroke:rgb(0,0,0);stroke-width:0.01" /> </g> 
  Visible = true
  X = 0
  Y = 0
  click1_x = 169.022
  click1_y = 176.901
FEATURE [Drawing::FeatureViewPython] grabPoint004  # drawing view (typed FeaturePython)
  Rotation = 0
  ViewResult = <g> <line x1="289.582382075" y1="121.545802544" x2="289.582382075" y2="121.545802544" style="stroke:rgb(0,0,0);stroke-width:0.01" /> </g> 
  Visible = true
  X = 0
  Y = 0
  click1_x = 289.582
  click1_y = 121.546
FEATURE [Drawing::FeatureViewPython] grabPoint005  # drawing view (typed FeaturePython)
  Rotation = 0
  ViewResult = <g> <line x1="171.188496614" y1="83.7227975387" x2="171.188496614" y2="83.7227975387" style="stroke:rgb(0,0,0);stroke-width:0.01" /> </g> 
  Visible = true
  X = 0
  Y = 0
  click1_x = 171.188
  click1_y = 83.7228
FEATURE [Drawing::FeatureViewPython] grabPoint006  # drawing view (typed FeaturePython)
  Rotation = 0
  ViewResult = <g> <line x1="181.038237501" y1="96.9214503272" x2="181.038237501" y2="96.9214503272" style="stroke:rgb(0,0,0);stroke-width:0.01" /> </g> 
  Visible = true
  X = 0
  Y = 0
  click1_x = 181.038
  click1_y = 96.9215
FEATURE [Drawing::FeatureViewPython] grabPoint007  # drawing view (typed FeaturePython)
  Rotation = 0
  ViewResult = <g> <line x1="180.25025823" y1="118.393885461" x2="180.25025823" y2="118.393885461" style="stroke:rgb(0,0,0);stroke-width:0.01" /> </g> 
  Visible = true
  X = 0
  Y = 0
  click1_x = 180.25
  click1_y = 118.394
FEATURE [Drawing::FeatureViewPython] weld001  # drawing view (typed FeaturePython)
  Rotation = 0
  ViewResult = <g   >\n<line x1="187.948207" y1="77.427168" x2="171.188497" y2="83.722798" style="stroke:rgb(0,0,255);stroke-width:0.50" />\n<polygon points="171.188497,83.722798 174.348541,83.603982 174.933024,82.316201 173.645243,81.731718" style="fill:rgb(0,0,255);stroke:rgb(0,0,255);stroke-width:0" />\n<line x1="187.948207" y1="77.427168" x2="203.308758" y2="77.427168" style="stroke:rgb(0,0,255);stroke-width:0.50" />\n</g> 
  Visible = true
  X = 0
  Y = 0
  arrowL1 = 3
  arrowL2 = 1
  arrowW = 2
  click1_x = 187.948
  click1_y = 77.4272
  click2_x = 203.309
  click2_y = 78.3013
  lineColor = rgb(0,0,255)
  strokeWidth = 0.5
  textRenderer_color = rgb(0,0,255)
  textRenderer_family = inherit
  textRenderer_size = 3.6
FEATURE [Drawing::FeatureViewPython] weld002  # drawing view (typed FeaturePython)
  Rotation = 0
  ViewResult = <g   >\n<line x1="188.073089" y1="77.427168" x2="181.038238" y2="96.921450" style="stroke:rgb(0,0,255);stroke-width:0.50" />\n<polygon points="181.038238,96.921450 182.997190,94.439011 182.396004,93.158942 181.115935,93.760127" style="fill:rgb(0,0,255);stroke:rgb(0,0,255);stroke-width:0" />\n<line x1="188.073089" y1="77.427168" x2="188.330694" y2="77.427168" style="stroke:rgb(0,0,255);stroke-width:0.50" />\n</g> 
  Visible = true
  X = 0
  Y = 0
  arrowL1 = 3
  arrowL2 = 1
  arrowW = 2
  click1_x = 188.073
  click1_y = 77.4272
  click2_x = 188.331
  click2_y = 77.6351
  lineColor = rgb(0,0,255)
  strokeWidth = 0.5
  textRenderer_color = rgb(0,0,255)
  textRenderer_family = inherit
  textRenderer_size = 3.6
FEATURE [Drawing::FeatureViewPython] weld003  # drawing view (typed FeaturePython)
  Rotation = 0
  ViewResult = <g   >\n<line x1="187.912688" y1="77.331106" x2="160.000000" y2="99.695000" style="stroke:rgb(0,0,255);stroke-width:0.50" />\n<polygon points="160.000000,99.695000 162.966495,98.599598 163.121634,97.193919 161.715955,97.038781" style="fill:rgb(0,0,255);stroke:rgb(0,0,255);stroke-width:0" />\n<line x1="187.912688" y1="77.331106" x2="187.993964" y2="77.331106" style="stroke:rgb(0,0,255);stroke-width:0.50" />\n</g> 
  Visible = true
  X = 0
  Y = 0
  arrowL1 = 3
  arrowL2 = 1
  arrowW = 2
  click1_x = 187.913
  click1_y = 77.3311
  click2_x = 187.994
  click2_y = 76.9193
  lineColor = rgb(0,0,255)
  strokeWidth = 0.5
  textRenderer_color = rgb(0,0,255)
  textRenderer_family = inherit
  textRenderer_size = 3.6
FEATURE [Drawing::FeatureViewPython] weld004  # drawing view (typed FeaturePython)
  Rotation = 0
  ViewResult = <g   >\n<line x1="195.398795" y1="162.110319" x2="179.462279" y2="146.761139" style="stroke:rgb(0,0,255);stroke-width:0.50" />\n<polygon points="179.462279,146.761139 180.929333,149.562523 182.343297,149.535978 182.316753,148.122014" style="fill:rgb(0,0,255);stroke:rgb(0,0,255);stroke-width:0" />\n<line x1="195.398795" y1="162.110319" x2="280.786016" y2="162.110319" style="stroke:rgb(0,0,255);stroke-width:0.50" />\n</g> 
  Visible = true
  X = 0
  Y = 0
  arrowL1 = 3
  arrowL2 = 1
  arrowW = 2
  click1_x = 195.399
  click1_y = 162.11
  click2_x = 280.786
  click2_y = 161.996
  lineColor = rgb(0,0,255)
  strokeWidth = 0.5
  textRenderer_color = rgb(0,0,255)
  textRenderer_family = inherit
  textRenderer_size = 3.6
FEATURE [Drawing::FeatureViewPython] weld005  # drawing view (typed FeaturePython)
  Rotation = 0
  ViewResult = <g   >\n<line x1="109.012041" y1="156.016438" x2="95.739481" y2="139.866321" style="stroke:rgb(0,0,255);stroke-width:0.50" />\n<polygon points="95.739481,139.866321 96.871671,142.818971 98.279169,142.956626 98.416824,141.549127" style="fill:rgb(0,0,255);stroke:rgb(0,0,255);stroke-width:0" />\n<line x1="109.012041" y1="156.016438" x2="118.031335" y2="156.016438" style="stroke:rgb(0,0,255);stroke-width:0.50" />\n</g> 
  Visible = true
  X = 0
  Y = 0
  arrowL1 = 3
  arrowL2 = 1
  arrowW = 2
  click1_x = 109.012
  click1_y = 156.016
  click2_x = 118.031
  click2_y = 155.67
  lineColor = rgb(0,0,255)
  strokeWidth = 0.5
  textRenderer_color = rgb(0,0,255)
  textRenderer_family = inherit
  textRenderer_size = 3.6
FEATURE [Drawing::FeatureViewPython] grabPoint008  # drawing view (typed FeaturePython)
  Rotation = 0
  ViewResult = <g> <line x1="83.0162337286" y1="122.875021446" x2="83.0162337286" y2="122.875021446" style="stroke:rgb(0,0,0);stroke-width:0.01" /> </g> 
  Visible = true
  X = 0
  Y = 0
  click1_x = 83.0162
  click1_y = 122.875
FEATURE [Drawing::FeatureViewPython] weld006  # drawing view (typed FeaturePython)
  Rotation = 0
  ViewResult = <g   >\n<line x1="96.320822" y1="110.834919" x2="83.016234" y2="122.875021" style="stroke:rgb(0,0,255);stroke-width:0.50" />\n<polygon points="83.016234,122.875021 85.911617,121.603504 85.982086,120.191047 84.569630,120.120578" style="fill:rgb(0,0,255);stroke:rgb(0,0,255);stroke-width:0" />\n<line x1="96.320822" y1="110.834919" x2="144.756121" y2="110.834919" style="stroke:rgb(0,0,255);stroke-width:0.50" />\n</g> 
  Visible = true
  X = 0
  Y = 0
  arrowL1 = 3
  arrowL2 = 1
  arrowW = 2
  click1_x = 96.3208
  click1_y = 110.835
  click2_x = 144.756
  click2_y = 110.89
  lineColor = rgb(0,0,255)
  strokeWidth = 0.5
  textRenderer_color = rgb(0,0,255)
  textRenderer_family = inherit
  textRenderer_size = 3.6
FEATURE [Drawing::FeatureViewPython] weld007  # drawing view (typed FeaturePython)
  Rotation = 0
  ViewResult = <g   >\n<line x1="192.839439" y1="191.694683" x2="169.021554" y2="176.901346" style="stroke:rgb(0,0,255);stroke-width:0.50" />\n<polygon points="169.021554,176.901346 171.042387,179.333677 172.419486,179.011809 172.097619,177.634710" style="fill:rgb(0,0,255);stroke:rgb(0,0,255);stroke-width:0" />\n<line x1="192.839439" y1="191.694683" x2="204.495142" y2="191.694683" style="stroke:rgb(0,0,255);stroke-width:0.50" />\n</g> 
  Visible = true
  X = 0
  Y = 0
  arrowL1 = 3
  arrowL2 = 1
  arrowW = 2
  click1_x = 192.839
  click1_y = 191.695
  click2_x = 204.495
  click2_y = 192.631
  lineColor = rgb(0,0,255)
  strokeWidth = 0.5
  textRenderer_color = rgb(0,0,255)
  textRenderer_family = inherit
  textRenderer_size = 3.6
FEATURE [Drawing::FeatureViewPython] weld008  # drawing view (typed FeaturePython)
  Rotation = 0
  ViewResult = <g   >\n<line x1="296.451467" y1="109.489023" x2="289.582382" y2="121.545803" style="stroke:rgb(0,0,255);stroke-width:0.50" />\n<polygon points="289.582382,121.545803 291.936335,119.434190 291.562481,118.070287 290.198577,118.444141" style="fill:rgb(0,0,255);stroke:rgb(0,0,255);stroke-width:0" />\n<line x1="296.451467" y1="109.489023" x2="305.991105" y2="109.489023" style="stroke:rgb(0,0,255);stroke-width:0.50" />\n</g> 
  Visible = true
  X = 0
  Y = 0
  arrowL1 = 3
  arrowL2 = 1
  arrowW = 2
  click1_x = 296.451
  click1_y = 109.489
  click2_x = 305.991
  click2_y = 109.778
  lineColor = rgb(0,0,255)
  strokeWidth = 0.5
  textRenderer_color = rgb(0,0,255)
  textRenderer_family = inherit
  textRenderer_size = 3.6
FEATURE [Drawing::FeatureViewPython] grabPoint009  # drawing view (typed FeaturePython)
  Rotation = 0
  ViewResult = <g> <line x1="210.99944027" y1="132.254067576" x2="210.99944027" y2="132.254067576" style="stroke:rgb(0,0,0);stroke-width:0.01" /> </g> 
  Visible = true
  X = 0
  Y = 0
  click1_x = 210.999
  click1_y = 132.254
FEATURE [Drawing::FeatureViewPython] grabPoint010  # drawing view (typed FeaturePython)
  Rotation = 0
  ViewResult = <g> <line x1="224.962000847" y1="123.841841638" x2="224.962000847" y2="123.841841638" style="stroke:rgb(0,0,0);stroke-width:0.01" /> </g> 
  Visible = true
  X = 0
  Y = 0
  click1_x = 224.962
  click1_y = 123.842
FEATURE [Drawing::FeatureViewPython] grabPoint011  # drawing view (typed FeaturePython)
  Rotation = 0
  ViewResult = <g> <line x1="213.167539738" y1="117.250819254" x2="213.167539738" y2="117.250819254" style="stroke:rgb(0,0,0);stroke-width:0.01" /> </g> 
  Visible = true
  X = 0
  Y = 0
  click1_x = 213.168
  click1_y = 117.251
FEATURE [Drawing::FeatureViewPython] weld009  # drawing view (typed FeaturePython)
  Rotation = 0
  ViewResult = <g   >\n<line x1="205.275658" y1="111.180141" x2="210.999440" y2="132.254068" style="stroke:rgb(0,0,255);stroke-width:0.50" />\n<polygon points="210.999440,132.254068 211.178151,129.096844 209.951004,128.393915 209.248075,129.621062" style="fill:rgb(0,0,255);stroke:rgb(0,0,255);stroke-width:0" />\n<line x1="205.275658" y1="111.180141" x2="195.909468" y2="111.180141" style="stroke:rgb(0,0,255);stroke-width:0.50" />\n</g> 
  Visible = true
  X = 0
  Y = 0
  arrowL1 = 3
  arrowL2 = 1
  arrowW = 2
  click1_x = 205.276
  click1_y = 111.18
  click2_x = 195.909
  click2_y = 112.134
  lineColor = rgb(0,0,255)
  strokeWidth = 0.5
  textRenderer_color = rgb(0,0,255)
  textRenderer_family = inherit
  textRenderer_size = 3.6
FEATURE [Drawing::FeatureViewPython] weld010  # drawing view (typed FeaturePython)
  Rotation = 0
  ViewResult = <g   >\n<line x1="222.290902" y1="108.398036" x2="213.167540" y2="117.250819" style="stroke:rgb(0,0,255);stroke-width:0.50" />\n<polygon points="213.167540,117.250819 216.016931,115.879335 216.038215,114.465281 214.624162,114.443997" style="fill:rgb(0,0,255);stroke:rgb(0,0,255);stroke-width:0" />\n<line x1="222.290902" y1="108.398036" x2="238.525631" y2="108.398036" style="stroke:rgb(0,0,255);stroke-width:0.50" />\n</g> 
  Visible = true
  X = 0
  Y = 0
  arrowL1 = 3
  arrowL2 = 1
  arrowW = 2
  click1_x = 222.291
  click1_y = 108.398
  click2_x = 238.526
  click2_y = 108.148
  lineColor = rgb(0,0,255)
  strokeWidth = 0.5
  textRenderer_color = rgb(0,0,255)
  textRenderer_family = inherit
  textRenderer_size = 3.6
FEATURE [Drawing::FeatureViewPython] weld011  # drawing view (typed FeaturePython)
  Rotation = 0
  ViewResult = <g   >\n<line x1="222.540667" y1="108.023388" x2="224.962001" y2="123.841842" style="stroke:rgb(0,0,255);stroke-width:0.50" />\n<polygon points="224.962001,123.841842 225.496564,120.725074 224.356770,119.887895 223.519591,121.027689" style="fill:rgb(0,0,255);stroke:rgb(0,0,255);stroke-width:0" />\n<line x1="222.540667" y1="108.023388" x2="222.415785" y2="108.023388" style="stroke:rgb(0,0,255);stroke-width:0.50" />\n</g> 
  Visible = true
  X = 0
  Y = 0
  arrowL1 = 3
  arrowL2 = 1
  arrowW = 2
  click1_x = 222.541
  click1_y = 108.023
  click2_x = 222.416
  click2_y = 108.398
  lineColor = rgb(0,0,255)
  strokeWidth = 0.5
  textRenderer_color = rgb(0,0,255)
  textRenderer_family = inherit
  textRenderer_size = 3.6
FEATURE [Drawing::FeatureViewPython] text002  # drawing view (typed FeaturePython)
  Rotation = 0
  ViewResult = <g> <text x="227.411086" y="106.275033" font-family="inherit" font-size="5" fill="rgb(0,0,0)" text-anchor="inherit" transform="rotate(0.000000 227.411086,106.275033)" >'B'</text> </g>
  Visible = true
  X = 0
  Y = 0
  click1_x = 227.411
  click1_y = 106.275
  rotation = 0
  text = 'B'
  textRenderer_addText_color = rgb(0,0,0)
  textRenderer_addText_family = inherit
  textRenderer_addText_size = 5
FEATURE [Drawing::FeaturePage] Page
  EditableTexts = AUTHOR NAME | CREATION DATE | SUPERVISOR NAME | CHECK DATE | SCALE | WEIGHT | NUMBER | SHEET | TITLE | SUBTITLE
  Group = -> [Ortho,Ortho001,Ortho002,Ortho004,Ortho005,Ortho006,text001,text003,text004,text005,text006,text007,text009,grabPoint001,grabPoint002,grabPoint003,grabPoint004,grabPoint005,grabPoint006,grabPoint007,weld001,weld002,weld003,weld004,weld005,grabPoint008,weld006,weld007,weld008,grabPoint009,grabPoint010,grabPoint011,weld009,weld010,weld011,text002]
FEATURE [Sketcher::SketchObject] Sketch071
  ExternalGeometry = -> [Pocket017]
  Placement = pos=(-60,0,0) rot=(0.57735,-0.57735,-0.57735;2.0944rad)
  Support = -> Pocket017 [Face78]
  sketch-geometry (1):
    g0: Circle CenterX=0 CenterY=65 CenterZ=0 NormalX=0 NormalY=0 NormalZ=1 Radius=2.5
  constraints (2):
    c: Coincident(g0,g-3)
    c: Radius(g0) = 2.5
FEATURE [PartDesign::Pad] Pad002
  Length = 8
  Length2 = 100
  Reversed = true
  Sketch = -> Sketch071
  Type = 0
FEATURE [Sketcher::SketchObject] Sketch072
  ExternalGeometry = -> [Pad002]
  Placement = pos=(0,0,70) rot=(0,0,1;0rad)
  Support = -> Pad002 [Face167]
  sketch-geometry (4):
    g0: Circle CenterX=-50 CenterY=0 CenterZ=0 NormalX=0 NormalY=0 NormalZ=1 Radius=5.3
    g1: ArcOfCircle CenterX=-50 CenterY=0 CenterZ=0 NormalX=0 NormalY=0 NormalZ=1 Radius=10 StartAngle=2.8682 EndAngle=3.14159
    g2: LineSegment StartX=-60 StartY=2.7 StartZ=0 EndX=-60 EndY=0 EndZ=0
    g3: LineSegment StartX=-60 StartY=2.7 StartZ=0 EndX=-59.6286 EndY=2.7 EndZ=0
  constraints (10):
    c: Coincident(g0,g-4)
    c: Coincident(g1,g0)
    c: Vertical(g2)
    c: Horizontal(g3)
    c: Equal(g0,g-3)
    c: PointOnObject(g-4,g1)
    c: Coincident(g2,g3)
    c: DistanceY(g0,g2) = 2.7
    c: Coincident(g1,g3)
    c: Coincident(g1,g2)
FEATURE [PartDesign::Pocket] Pocket018
  Length = 8
  Sketch = -> Sketch072
  Type = 0
FEATURE [Sketcher::SketchObject] Sketch073
  ExternalGeometry = -> [Pocket018]
  Placement = pos=(-60,0,0) rot=(0.57735,-0.57735,-0.57735;2.0944rad)
  Support = -> Pocket018 [Face90]
  sketch-geometry (2):
    g0: LineSegment [constr] StartX=0 StartY=75.8704 StartZ=0 EndX=0 EndY=60.9078 EndZ=0
    g1: Circle CenterX=0 CenterY=64.1 CenterZ=0 NormalX=0 NormalY=0 NormalZ=1 Radius=2.2
  constraints (5):
    c: Vertical(g0)
    c: PointOnObject(g-3,g0)
    c: PointOnObject(g1,g0)
    c: DistanceY(g1,g-3) = 0.9
    c: Equal(g-3,g1)
FEATURE [PartDesign::Pocket] Pocket019
  Length = 8
  Sketch = -> Sketch073
  Type = 0
FEATURE [Part::Mirroring] Part__Mirroring  label="Pocket019 (Mirror #1)"
  Base = (0,0,0)
  Normal = (0,1,0)
  Source = -> Pocket019
FEATURE [Sketcher::SketchObject] Sketch074
  ExternalGeometry = -> [Pocket019]
  Placement = pos=(-62.5,0,0) rot=(0.57735,0.57735,0.57735;2.0944rad)
  Support = -> Pocket019 [Face281]
  sketch-geometry (4):
    g0: Circle CenterX=-18 CenterY=43.5 CenterZ=0 NormalX=0 NormalY=0 NormalZ=1 Radius=6
    g1: Circle CenterX=-18 CenterY=43.5 CenterZ=0 NormalX=0 NormalY=0 NormalZ=1 Radius=3
    g2: Circle CenterX=-18 CenterY=23.5 CenterZ=0 NormalX=0 NormalY=0 NormalZ=1 Radius=6
    g3: Circle CenterX=-18 CenterY=23.5 CenterZ=0 NormalX=0 NormalY=0 NormalZ=1 Radius=3
  constraints (8):
    c: Coincident(g0,g-4)
    c: Coincident(g1,g0)
    c: Coincident(g2,g-6)
    c: Coincident(g3,g2)
    c: Equal(g0,g-3)
    c: Equal(g-3,g2)
    c: Equal(g3,g-5)
    c: Equal(g-5,g1)
FEATURE [PartDesign::Pad] Pad003
  Length = 1
  Length2 = 100
  Sketch = -> Sketch074
  Type = 0
FEATURE [Sketcher::SketchObject] Sketch075
  ExternalGeometry = -> [Pad003]
  Placement = pos=(-60,0,0) rot=(0.57735,0.57735,0.57735;2.0944rad)
  Support = -> Pad003 [Face189]
  sketch-geometry (1):
    g0: Circle CenterX=-18 CenterY=43.5 CenterZ=0 NormalX=0 NormalY=0 NormalZ=1 Radius=6
  constraints (2):
    c: Coincident(g0,g-3)
    c: Equal(g0,g-3)
FEATURE [PartDesign::Pocket] Pocket020
  Length = 5
  Reversed = true
  Sketch = -> Sketch075
  Type = 0
FEATURE [Sketcher::SketchObject] Sketch076
  ExternalGeometry = -> [Pocket020]
  Placement = pos=(62.5,0,0) rot=(0.57735,-0.57735,-0.57735;2.0944rad)
  Support = -> Pocket020 [Face272]
  sketch-geometry (4):
    g0: Circle CenterX=18 CenterY=43.5 CenterZ=0 NormalX=0 NormalY=0 NormalZ=1 Radius=6
    g1: Circle CenterX=18 CenterY=43.5 CenterZ=0 NormalX=0 NormalY=0 NormalZ=1 Radius=3
    g2: Circle CenterX=18 CenterY=23.5 CenterZ=0 NormalX=0 NormalY=0 NormalZ=1 Radius=6
    g3: Circle CenterX=18 CenterY=23.5 CenterZ=0 NormalX=0 NormalY=0 NormalZ=1 Radius=3
  constraints (8):
    c: Coincident(g0,g-6)
    c: Coincident(g1,g0)
    c: Coincident(g2,g-4)
    c: Coincident(g3,g2)
    c: Equal(g-3,g2)
    c: Equal(g2,g0)
    c: Equal(g3,g-4)
    c: Equal(g-4,g1)
FEATURE [PartDesign::Pad] Pad004
  Length = 1
  Length2 = 100
  Sketch = -> Sketch076
  Type = 0
FEATURE [Sketcher::SketchObject] Sketch077
  ExternalGeometry = -> [Pad004]
  Placement = pos=(60,0,0) rot=(0.57735,-0.57735,-0.57735;2.0944rad)
  Support = -> Pad004 [Face111]
  sketch-geometry (1):
    g0: Circle CenterX=18 CenterY=43.5 CenterZ=0 NormalX=0 NormalY=0 NormalZ=1 Radius=6
  constraints (2):
    c: Coincident(g0,g-3)
    c: Equal(g0,g-3)
FEATURE [PartDesign::Pocket] Pocket021
  Length = 5
  Reversed = true
  Sketch = -> Sketch077
  Type = 0
FEATURE [Sketcher::SketchObject] Sketch078
  ExternalGeometry = -> [Pocket021]
  Placement = pos=(0,0,70) rot=(0,0,1;0rad)
  Support = -> Pocket021 [Face170]
  sketch-geometry (2):
    g0: Circle CenterX=-50 CenterY=0 CenterZ=0 NormalX=0 NormalY=0 NormalZ=1 Radius=6
    g1: Circle CenterX=-50 CenterY=0 CenterZ=0 NormalX=0 NormalY=0 NormalZ=1 Radius=5.2
  constraints (4):
    c: Coincident(g0,g-3)
    c: Coincident(g1,g0)
    c: Radius(g0) = 6
    c: Radius(g1) = 5.2
FEATURE [PartDesign::Pad] Pad005
  Length = 16
  Length2 = 100
  Reversed = true
  Sketch = -> Sketch078
  Type = 0
FEATURE [Sketcher::SketchObject] Sketch079
  ExternalGeometry = -> [Pad005]
  Placement = pos=(0,0,0) rot=(1,0,0;3.14159rad)
  Support = -> Pad005 [Face248]
  sketch-geometry (2):
    g0: Circle CenterX=-50 CenterY=0 CenterZ=0 NormalX=0 NormalY=0 NormalZ=1 Radius=7.5
    g1: Circle CenterX=-50 CenterY=0 CenterZ=0 NormalX=0 NormalY=0 NormalZ=1 Radius=5.3
  constraints (4):
    c: Coincident(g0,g-3)
    c: Coincident(g1,g0)
    c: Radius(g0) = 7.5
    c: Radius(g1) = 5.3
FEATURE [PartDesign::Pad] Pad006
  Length = 11.25
  Length2 = 100
  Reversed = true
  Sketch = -> Sketch079
  Type = 0
FEATURE [Sketcher::SketchObject] Sketch080
  ExternalGeometry = -> [Pad006]
  Placement = pos=(-60,0,0) rot=(0.57735,-0.57735,-0.57735;2.0944rad)
  Support = -> Pad006 [Face92]
  sketch-geometry (1):
    g0: Circle CenterX=0 CenterY=64.1 CenterZ=0 NormalX=0 NormalY=0 NormalZ=1 Radius=2.2
  constraints (2):
    c: Coincident(g0,g-3)
    c: PointOnObject(g-3,g0)
FEATURE [PartDesign::Pocket] Pocket022
  Length = 8
  Sketch = -> Sketch080
  Type = 0
